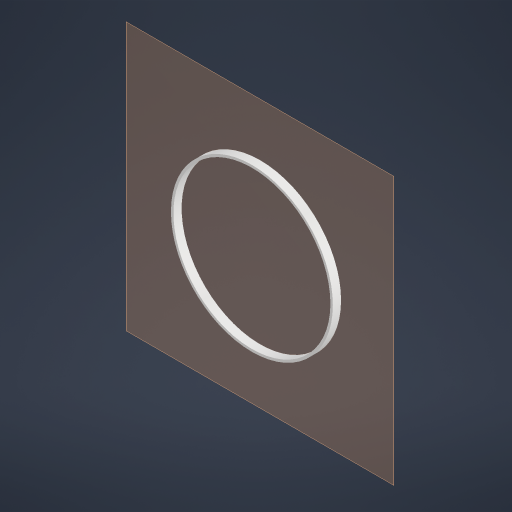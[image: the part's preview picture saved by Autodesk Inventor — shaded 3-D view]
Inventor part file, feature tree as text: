
AUTODESK INVENTOR PART (.ipt)
format: ipt  version: 2023.1 (Build 271208000, 208)  size: 178,688 bytes
history: native  units: mm
features: other x3, plane x1, extrude x1, sketch x1
ambient origin geometry x8: Origin, YZ Plane, XZ Plane, XY Plane, X Axis, Y Axis, Z Axis, Center Point
bodies: Solid1 (feature_tree)
feature tree (6):
  plane  "Work Plane1"
  extrude  "Extrusion1"  Depth=10.0mm
  sketch  "Sketch1"  dims[d0=190.985932mm d1=3.0mm d2=10.0mm d3=0.0mm]
  parser-record x1  (decoder bookkeeping rows leaked as tree rows — omitted from the tree; the rows remain in map.json)
  other  "Beau4tClock.iam"
  other  "Clock:1"
note: 1 file-system path scrubbed to <path> (originals preserved in map.json)
